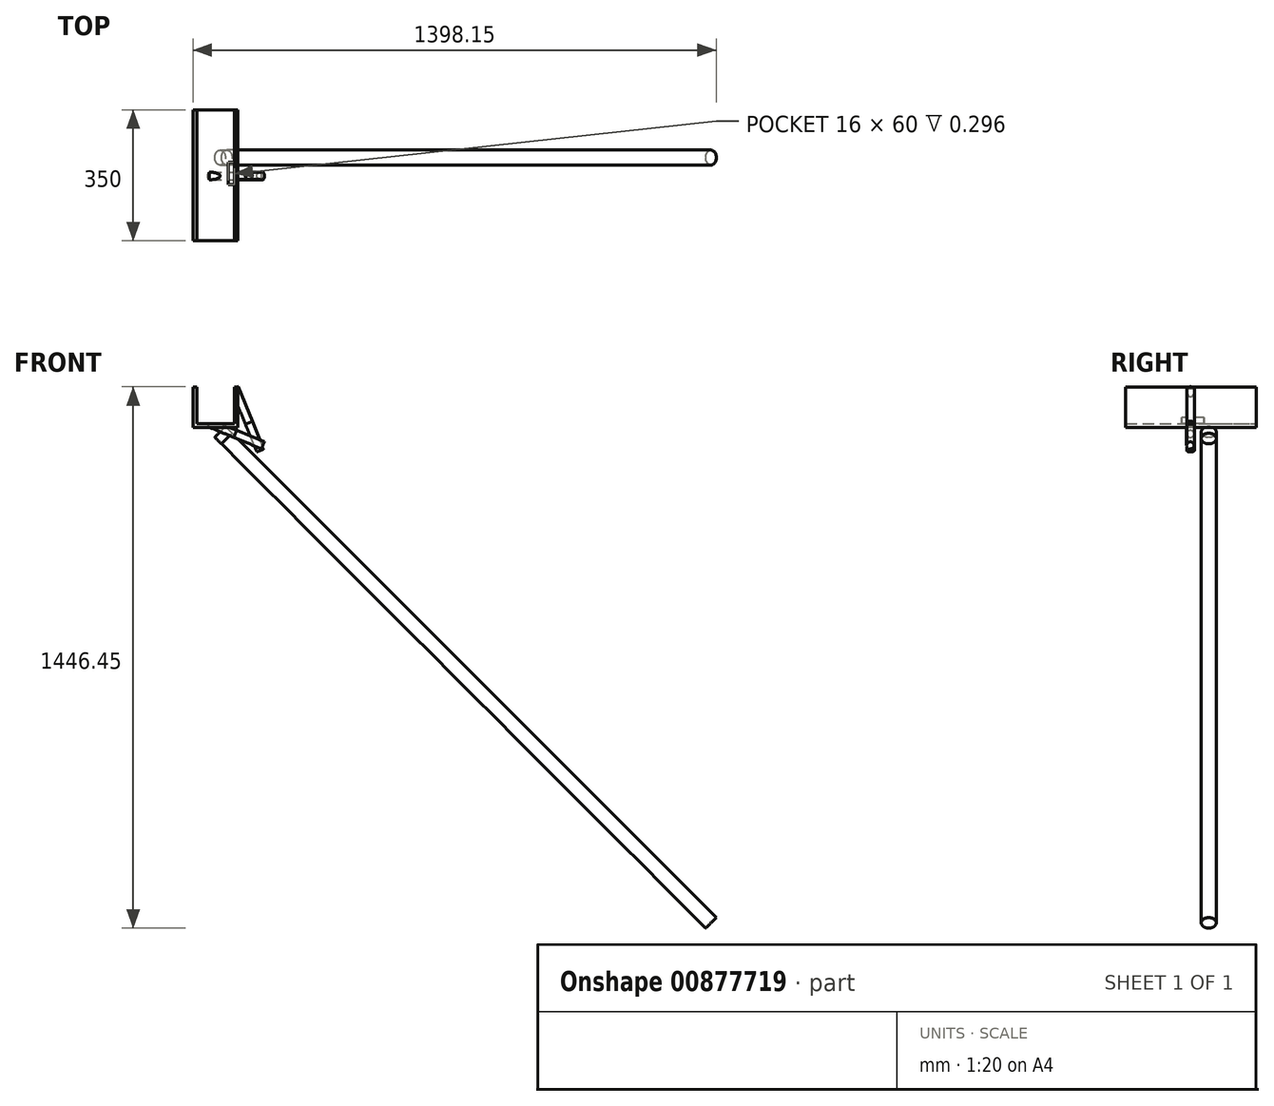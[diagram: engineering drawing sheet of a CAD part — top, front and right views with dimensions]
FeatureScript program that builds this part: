
annotation { "Feature Type Name" : "Feature", "Feature Type Description" : "" }
export const myFeature = defineFeature(function(context is Context, id is Id, definition is map)
    precondition{}
    {
        {
            var Q0;
            Q0=qCreatedBy(makeId("Top.planeOp"),FACE);
            var sketch = newSketch(context, id + "F0", { "sketchPlane" : qUnion([Q0])});
            skLineSegment(sketch, "E0.bottom", {"start": v(60, 175) * mm, "end": v(-60, 175) * mm});
            skLineSegment(sketch, "E0.top", {"start": v(60, -175) * mm, "end": v(-60, -175) * mm});
            skLineSegment(sketch, "E0.left", {"start": v(60, 175) * mm, "end": v(60, -175) * mm});
            skLineSegment(sketch, "E0.right", {"start": v(-60, 175) * mm, "end": v(-60, -175) * mm});
            skPoint(sketch, "E0.middle", {"position": v(0, 0) * mm});
            skSolve(sketch);
        }
        {
            var Q0;
            Q0 = qSketchRegion(id + "F0", true);
            extrude(context, id + "F1", {"entities" : qUnion([Q0]), "depth" : 10 * mm, "offsetDistance" : 25 * mm});
        }
        {
            var Q0;
            Q0=makeQuery(id+"F1.opExtrude","CAP_FACE",FACE,{"disambiguationData":[OSD([sQuery(id+"F0.wireOp",EDGE,"E0.bottom"),sQuery(id+"F0.wireOp",EDGE,"E0.top"),sQuery(id+"F0.wireOp",EDGE,"E0.left"),sQuery(id+"F0.wireOp",EDGE,"E0.right")])],"isStart":false});
            var sketch = newSketch(context, id + "F2", { "sketchPlane" : qUnion([Q0])});
            skLineSegment(sketch, "E1.bottom", {"start": v(-60, -175) * mm, "end": v(-50, -175) * mm});
            skLineSegment(sketch, "E1.top", {"start": v(-60, 175) * mm, "end": v(-50, 175) * mm});
            skLineSegment(sketch, "E1.left", {"start": v(-60, -175) * mm, "end": v(-60, 175) * mm});
            skLineSegment(sketch, "E1.right", {"start": v(-50, -175) * mm, "end": v(-50, 175) * mm});
            skLineSegment(sketch, "E2.bottom", {"start": v(60, 175) * mm, "end": v(50, 175) * mm});
            skLineSegment(sketch, "E2.top", {"start": v(60, -175) * mm, "end": v(50, -175) * mm});
            skLineSegment(sketch, "E2.left", {"start": v(60, 175) * mm, "end": v(60, -175) * mm});
            skLineSegment(sketch, "E2.right", {"start": v(50, 175) * mm, "end": v(50, -175) * mm});
            skSolve(sketch);
        }
        {
            var Q0;
            Q0=makeQuery(id+"F2.imprint","IMPRINT",FACE,{"disambiguationData":[TD([[makeQuery(id+"F2.imprint","IMPRINT",EDGE,{"derivedFrom":sQuery(id+"F2.wireOp",EDGE,"E1.bottom")}),-1.0]])]});
            var sketch = newSketch(context, id + "F3", { "sketchPlane" : qUnion([Q0])});
            skSolve(sketch);
        }
        {
            var Q0;
            Q0=makeQuery(id+"F2.imprint","IMPRINT",FACE,{"disambiguationData":[TD([[makeQuery(id+"F2.imprint","IMPRINT",EDGE,{"derivedFrom":sQuery(id+"F2.wireOp",EDGE,"E2.bottom")}),1.0]])]});
            extrude(context, id + "F4", {"entities" : qUnion([Q0]), "operationType" : NewBodyOperationType.ADD, "depth" : 98 * mm, "offsetDistance" : 25 * mm});
        }
        {
            var Q0;
            Q0=makeQuery(id+"F3.imprint","IMPRINT",FACE,{"disambiguationData":[TD([[makeQuery(id+"F3.imprint","IMPRINT",EDGE,{"derivedFrom":makeQuery(id+"F2.imprint","IMPRINT",EDGE,{"derivedFrom":sQuery(id+"F2.wireOp",EDGE,"E1.bottom")})}),-1.0]])]});
            extrude(context, id + "F5", {"entities" : qUnion([Q0]), "operationType" : NewBodyOperationType.ADD, "depth" : 98 * mm, "offsetDistance" : 25 * mm});
        }
        {
            var Q0;
            Q0=makeQuery(id+"F1.opExtrude","CAP_EDGE",EDGE,{"disambiguationData":[OSD([sQuery(id+"F0.wireOp",EDGE,"E0.left")])],"isStart":true});
            cPlane(context, id + "F6", {"entities" : qUnion([Q0]), "cplaneType" : CPlaneType.LINE_ANGLE, "offset" : 25 * mm, "angle" : 45 * degree, "width" : 150 * mm, "height" : 150 * mm});
        }
        {
            var Q0;
            Q0=qCreatedBy(id+"F6.planeOp",FACE);
            var sketch = newSketch(context, id + "F7", { "sketchPlane" : qUnion([Q0])});
            skCircle(sketch, "E3", {"center": v(47.36, 0) * mm, "radius": 20 * mm});
            skSolve(sketch);
        }
        {
            var Q0;
            Q0=makeQuery(id+"F7.imprint","IMPRINT",FACE,{"disambiguationData":[TD([[makeQuery(id+"F7.imprint","IMPRINT",EDGE,{"derivedFrom":sQuery(id+"F7.wireOp",EDGE,"E3")}),1.0]])]});
            extrude(context, id + "F8", {"entities" : qUnion([Q0]), "depth" : 1830 * mm, "offsetDistance" : 25 * mm});
        }
        {
            var Q0;
            Q0=makeQuery(id+"F8.opExtrude","CAP_FACE",FACE,{"disambiguationData":[OSD([sQuery(id+"F7.wireOp",EDGE,"E3")])],"isStart":true});
            extrude(context, id + "F9", {"entities" : qUnion([Q0]), "depth" : 25 * mm, "offsetDistance" : 25 * mm});
        }
        {
            var Q0;
            Q0=qCreatedBy(makeId("Front.planeOp"),FACE);
            cPlane(context, id + "F10", {"entities" : qUnion([Q0]), "cplaneType" : CPlaneType.OFFSET, "offset" : 25 * mm, "width" : 150 * mm, "height" : 150 * mm});
        }
        {
            var Q0;
            Q0=qCreatedBy(id+"F10.planeOp",FACE);
            var sketch = newSketch(context, id + "F11", { "sketchPlane" : qUnion([Q0])});
            skLineSegment(sketch, "E4.bottom", {"start": v(50.3, 9.7) * mm, "end": v(34.3, 9.7) * mm});
            skLineSegment(sketch, "E4.top", {"start": v(50.3, 25.9) * mm, "end": v(34.3, 25.9) * mm});
            skLineSegment(sketch, "E4.left", {"start": v(50.3, 9.7) * mm, "end": v(50.3, 25.9) * mm});
            skLineSegment(sketch, "E4.right", {"start": v(34.3, 9.7) * mm, "end": v(34.3, 25.9) * mm});
            skSolve(sketch);
        }
        {
            var Q0;
            Q0=makeQuery(id+"F11.imprint","IMPRINT",FACE,{"disambiguationData":[TD([[makeQuery(id+"F11.imprint","IMPRINT",EDGE,{"derivedFrom":sQuery(id+"F11.wireOp",EDGE,"E4.bottom")}),-1.0]])]});
            extrude(context, id + "F12", {"entities" : qUnion([Q0]), "operationType" : NewBodyOperationType.REMOVE, "oppositeDirection" : true, "depth" : 60 * mm, "offsetDistance" : 25 * mm});
        }
        {
            var Q0;
            Q0=makeQuery(id+"F1.opExtrude","CAP_EDGE",EDGE,{"disambiguationData":[OSD([sQuery(id+"F0.wireOp",EDGE,"E0.left")])],"isStart":true});
            cPlane(context, id + "F13", {"entities" : qUnion([Q0]), "cplaneType" : CPlaneType.LINE_ANGLE, "offset" : 25 * mm, "angle" : 22.5 * degree, "width" : 150 * mm, "height" : 150 * mm});
        }
        {
            var Q0;
            Q0=makeQuery(id+"F1.opExtrude","CAP_EDGE",EDGE,{"disambiguationData":[OSD([sQuery(id+"F0.wireOp",EDGE,"E0.left")])],"isStart":true});
            cPlane(context, id + "F14", {"entities" : qUnion([Q0]), "cplaneType" : CPlaneType.LINE_ANGLE, "offset" : 25 * mm, "angle" : 67.5 * degree, "width" : 150 * mm, "height" : 150 * mm});
        }
        {
            var Q0;
            Q0=qCreatedBy(id+"F13.planeOp",FACE);
            var sketch = newSketch(context, id + "F15", { "sketchPlane" : qUnion([Q0])});
            skCircle(sketch, "E5", {"center": v(87.02, 1.3) * mm, "radius": 10 * mm});
            skSolve(sketch);
        }
        {
            var Q0;
            Q0=makeQuery(id+"F15.imprint","IMPRINT",FACE,{"disambiguationData":[TD([[makeQuery(id+"F15.imprint","IMPRINT",EDGE,{"derivedFrom":sQuery(id+"F15.wireOp",EDGE,"E5")}),1.0]])]});
            extrude(context, id + "F16", {"entities" : qUnion([Q0]), "oppositeDirection" : true, "depth" : 100 * mm, "offsetDistance" : 25 * mm});
        }
        {
            var Q0;
            Q0=makeQuery(id+"F16.opExtrude","CAP_FACE",FACE,{"disambiguationData":[OSD([sQuery(id+"F15.wireOp",EDGE,"E5")])],"isStart":true});
            extrude(context, id + "F17", {"entities" : qUnion([Q0]), "depth" : 80 * mm, "offsetDistance" : 25 * mm});
        }
        {
            var Q0;
            Q0=qCreatedBy(id+"F14.planeOp",FACE);
            var sketch = newSketch(context, id + "F18", { "sketchPlane" : qUnion([Q0])});
            skCircle(sketch, "E6", {"center": v(-1.73, 3.96) * mm, "radius": 10 * mm});
            skSolve(sketch);
        }
        {
            var Q0;
            Q0=makeQuery(id+"F18.imprint","IMPRINT",FACE,{"disambiguationData":[TD([[makeQuery(id+"F18.imprint","IMPRINT",EDGE,{"derivedFrom":sQuery(id+"F18.wireOp",EDGE,"E6")}),1.0]])]});
            extrude(context, id + "F19", {"entities" : qUnion([Q0]), "depth" : 80 * mm, "offsetDistance" : 25 * mm});
        }
        {
            var Q0;
            Q0=makeQuery(id+"F19.opExtrude","CAP_FACE",FACE,{"disambiguationData":[OSD([sQuery(id+"F18.wireOp",EDGE,"E6")])],"isStart":true});
            extrude(context, id + "F20", {"entities" : qUnion([Q0]), "depth" : 75 * mm, "offsetDistance" : 25 * mm});
        }
        {
            var Q0;
            Q0=makeQuery(id+"F5.boolean.opBoolean","MERGE",FACE,{"derivedFrom":[makeQuery(id+"F4.boolean.opBoolean","MERGE",FACE,{"derivedFrom":[makeQuery(id+"F1.opExtrude","SWEPT_FACE",FACE,{"disambiguationData":[OSD([sQuery(id+"F0.wireOp",EDGE,"E0.bottom")])]}),makeQuery(id+"F4.opExtrude","SWEPT_FACE",FACE,{"disambiguationData":[OSD([sQuery(id+"F2.wireOp",EDGE,"E2.bottom")])]})]}),makeQuery(id+"F5.opExtrude","SWEPT_FACE",FACE,{"disambiguationData":[OSD([sQuery(id+"F2.wireOp",EDGE,"E1.top")])]})]});
            cPlane(context, id + "F21", {"entities" : qUnion([Q0]), "cplaneType" : CPlaneType.OFFSET, "offset" : 0 * mm, "width" : 150 * mm, "height" : 150 * mm});
        }
        {
            var Q0;
            Q0=qCreatedBy(id+"F21.planeOp",FACE);
            var sketch = newSketch(context, id + "F22", { "sketchPlane" : qUnion([Q0])});
            skLineSegment(sketch, "E7.bottom", {"start": v(-50, 10) * mm, "end": v(50, 10) * mm});
            skLineSegment(sketch, "E7.top", {"start": v(-50, 108) * mm, "end": v(50, 108) * mm});
            skLineSegment(sketch, "E7.left", {"start": v(-50, 10) * mm, "end": v(-50, 108) * mm});
            skLineSegment(sketch, "E7.right", {"start": v(50, 10) * mm, "end": v(50, 108) * mm});
            skSolve(sketch);
        }
        {
            var Q0;
            Q0 = qSketchRegion(id + "F22", true);
            extrude(context, id + "F23", {"entities" : qUnion([Q0]), "operationType" : NewBodyOperationType.REMOVE, "oppositeDirection" : true, "depth" : 200 * mm, "offsetDistance" : 25 * mm});
        }
    });
